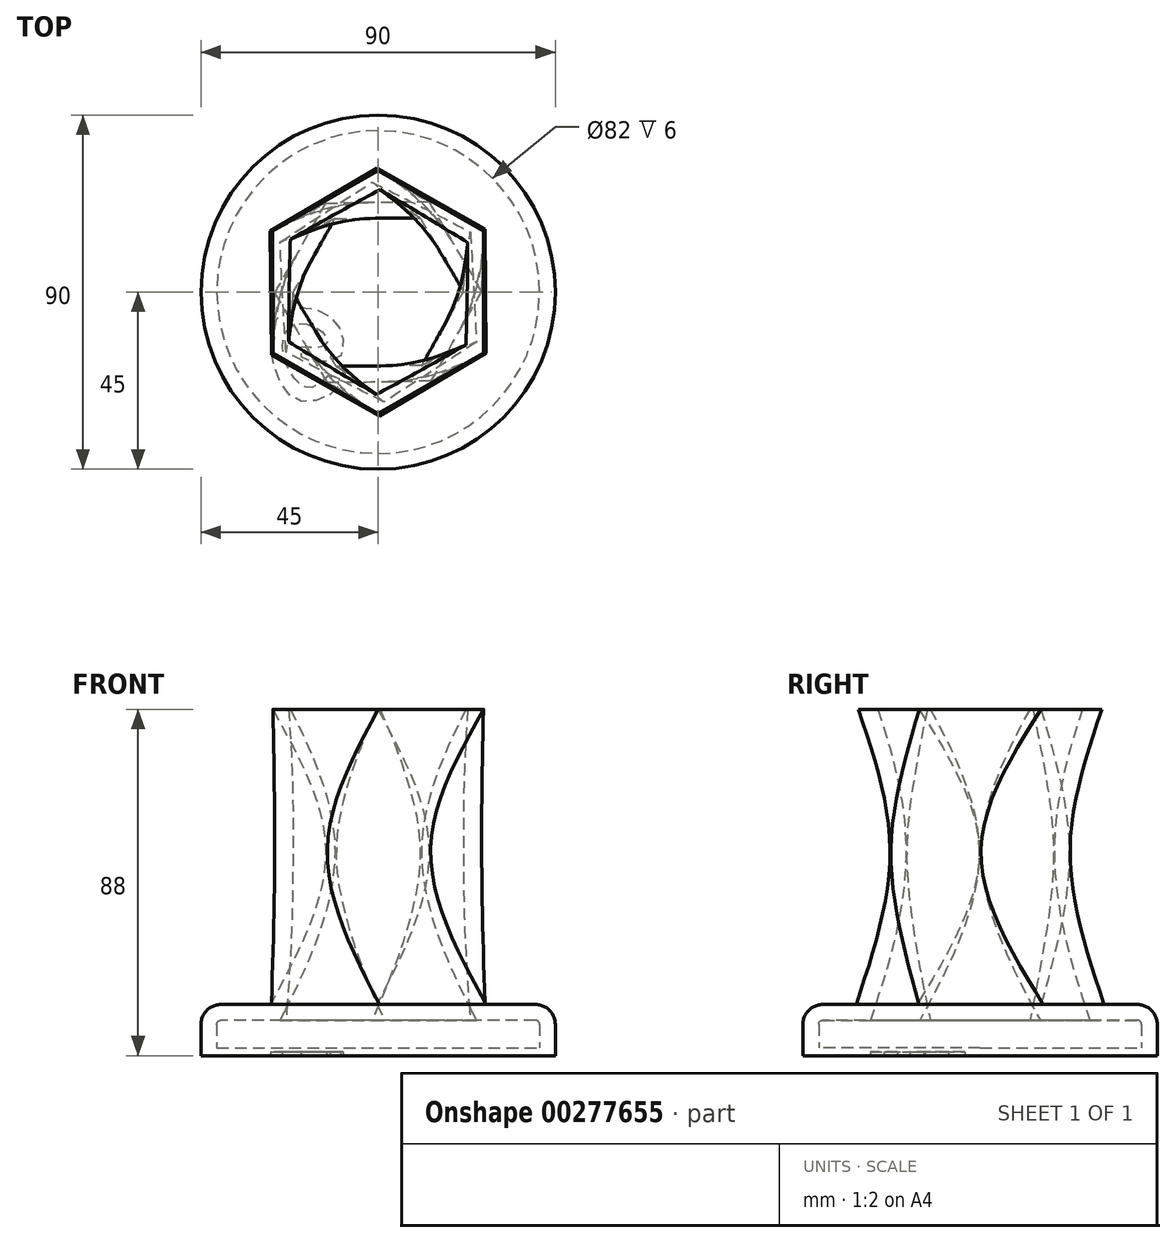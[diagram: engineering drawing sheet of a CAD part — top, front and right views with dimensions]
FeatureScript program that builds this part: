
annotation { "Feature Type Name" : "Feature", "Feature Type Description" : "" }
export const myFeature = defineFeature(function(context is Context, id is Id, definition is map)
    precondition{}
    {
        {
            var Q0;
            Q0=qCreatedBy(makeId("Top.planeOp"),FACE);
            var sketch = newSketch(context, id + "F0", { "sketchPlane" : qUnion([Q0])});
            skCircle(sketch, "E0", {"center": v(0, 0) * mm, "radius": 45 * mm});
            skSolve(sketch);
        }
        {
            var Q0;
            Q0 = qSketchRegion(id + "F0", true);
            extrude(context, id + "F1", {"entities" : qUnion([Q0]), "depth" : 15 * mm});
        }
        {
            var Q0;
            Q0=makeQuery(id+"F1.opExtrude","CAP_EDGE",EDGE,{"disambiguationData":[OSD([sQuery(id+"F0.wireOp",EDGE,"E0")])],"isStart":false});
            fillet(context, id + "F2", {"entities" : qUnion([Q0]), "radius" : 5 * mm, "tangentPropagation" : true, "allowEdgeOverflow" : false});
        }
        {
            var Q0;
            Q0=qCreatedBy(makeId("Top.planeOp"),FACE);
            cPlane(context, id + "F3", {"entities" : qUnion([Q0]), "cplaneType" : CPlaneType.OFFSET, "offset" : 15 * mm, "width" : 150 * mm, "height" : 150 * mm});
        }
        {
            var Q0;
            Q0=qCreatedBy(id+"F3.planeOp",FACE);
            var sketch = newSketch(context, id + "F4", { "sketchPlane" : qUnion([Q0])});
            skCircle(sketch, "E1.cCircle", {"center": v(0, 0) * mm, "radius": 27.26 * mm, "construction": true});
            skLineSegment(sketch, "E1.0", {"start": v(-0.3, 31.48) * mm, "end": v(27.1, 16) * mm});
            skLineSegment(sketch, "E1.1", {"start": v(27.1, 16) * mm, "end": v(27.4, -15.48) * mm});
            skLineSegment(sketch, "E1.2", {"start": v(27.4, -15.48) * mm, "end": v(0.3, -31.48) * mm});
            skLineSegment(sketch, "E1.3", {"start": v(0.3, -31.48) * mm, "end": v(-27.1, -16) * mm});
            skLineSegment(sketch, "E1.4", {"start": v(-27.1, -16) * mm, "end": v(-27.4, 15.48) * mm});
            skLineSegment(sketch, "E1.5", {"start": v(-27.4, 15.48) * mm, "end": v(-0.3, 31.48) * mm});
            skPoint(sketch, "E1.0.midPoint", {"position": v(13.4, 23.74) * mm});
            skSolve(sketch);
        }
        {
            var Q0;
            Q0=qCreatedBy(id+"F3.planeOp",FACE);
            cPlane(context, id + "F5", {"entities" : qUnion([Q0]), "cplaneType" : CPlaneType.OFFSET, "offset" : 40 * mm, "width" : 150 * mm, "height" : 150 * mm});
        }
        {
            var Q0;
            Q0=qCreatedBy(id+"F5.planeOp",FACE);
            var sketch = newSketch(context, id + "F6", { "sketchPlane" : qUnion([Q0])});
            skCircle(sketch, "E2.cCircle", {"center": v(0, 0) * mm, "radius": 22.76 * mm, "construction": true});
            skLineSegment(sketch, "E2.0", {"start": v(26.28, 0.28) * mm, "end": v(13.38, -22.62) * mm});
            skLineSegment(sketch, "E2.1", {"start": v(13.38, -22.62) * mm, "end": v(-12.9, -22.9) * mm});
            skLineSegment(sketch, "E2.2", {"start": v(-12.9, -22.9) * mm, "end": v(-26.28, -0.28) * mm});
            skLineSegment(sketch, "E2.3", {"start": v(-26.28, -0.28) * mm, "end": v(-13.38, 22.62) * mm});
            skLineSegment(sketch, "E2.4", {"start": v(-13.38, 22.62) * mm, "end": v(12.9, 22.9) * mm});
            skLineSegment(sketch, "E2.5", {"start": v(12.9, 22.9) * mm, "end": v(26.28, 0.28) * mm});
            skPoint(sketch, "E2.0.midPoint", {"position": v(19.83, -11.17) * mm});
            skSolve(sketch);
        }
        {
            var Q0;
            Q0=qCreatedBy(id+"F5.planeOp",FACE);
            cPlane(context, id + "F7", {"entities" : qUnion([Q0]), "cplaneType" : CPlaneType.OFFSET, "offset" : 35 * mm, "width" : 150 * mm, "height" : 150 * mm});
        }
        {
            var Q0;
            Q0=qCreatedBy(id+"F7.planeOp",FACE);
            var sketch = newSketch(context, id + "F8", { "sketchPlane" : qUnion([Q0])});
            skCircle(sketch, "E3.cCircle", {"center": v(0, 0) * mm, "radius": 26.78 * mm, "construction": true});
            skLineSegment(sketch, "E3.0", {"start": v(26.79, -15.44) * mm, "end": v(0.02, -30.92) * mm});
            skLineSegment(sketch, "E3.1", {"start": v(0.02, -30.92) * mm, "end": v(-26.76, -15.48) * mm});
            skLineSegment(sketch, "E3.2", {"start": v(-26.76, -15.48) * mm, "end": v(-26.79, 15.44) * mm});
            skLineSegment(sketch, "E3.3", {"start": v(-26.79, 15.44) * mm, "end": v(-0.02, 30.92) * mm});
            skLineSegment(sketch, "E3.4", {"start": v(-0.02, 30.92) * mm, "end": v(26.76, 15.48) * mm});
            skLineSegment(sketch, "E3.5", {"start": v(26.76, 15.48) * mm, "end": v(26.79, -15.44) * mm});
            skPoint(sketch, "E3.0.midPoint", {"position": v(13.4, -23.18) * mm});
            skSolve(sketch);
        }
        {
            var Q1;
            Q1=makeQuery(id+"F8.imprint","IMPRINT",FACE,{"disambiguationData":[TD([[makeQuery(id+"F8.imprint","IMPRINT",EDGE,{"derivedFrom":sQuery(id+"F8.wireOp",EDGE,"E3.0")}),-1.0]])]});
            var Q2;
            Q2=makeQuery(id+"F6.imprint","IMPRINT",FACE,{"disambiguationData":[TD([[makeQuery(id+"F6.imprint","IMPRINT",EDGE,{"derivedFrom":sQuery(id+"F6.wireOp",EDGE,"E2.0")}),-1.0]])]});
            var Q3;
            Q3=makeQuery(id+"F4.imprint","IMPRINT",FACE,{"disambiguationData":[TD([[makeQuery(id+"F4.imprint","IMPRINT",EDGE,{"derivedFrom":sQuery(id+"F4.wireOp",EDGE,"E1.0")}),-1.0]])]});
            loft(context, id + "F9", {"operationType" : NewBodyOperationType.ADD, "sheetProfilesArray" : [{ "sheetProfileEntities" : qUnion([Q1]) }, { "sheetProfileEntities" : qUnion([Q2]) }, { "sheetProfileEntities" : qUnion([Q3]) }]});
        }
        {
            var Q0;
            Q0=makeQuery(id+"F9.opLoft","CAP_FACE",FACE,{"disambiguationData":[OSD([makeQuery(id+"F8.imprint","IMPRINT",FACE,{"disambiguationData":[TD([[makeQuery(id+"F8.imprint","IMPRINT",EDGE,{"derivedFrom":sQuery(id+"F8.wireOp",EDGE,"E3.0")}),-1.0]])]})])],"isStart":true});
            shell(context, id + "F10", {"entities" : qUnion([Q0]), "thickness" : 4 * mm});
        }
        {
            var Q0;
            Q0=makeQuery(id+"F1.opExtrude","CAP_FACE",FACE,{"disambiguationData":[OSD([sQuery(id+"F0.wireOp",EDGE,"E0")])],"isStart":true});
            var sketch = newSketch(context, id + "F11", { "sketchPlane" : qUnion([Q0])});
            skFitSpline(sketch, "E4", {"points": [v(-19.62, 5.51) * mm, v(-3.35, 33.08) * mm, v(0, 13.82) * mm, v(15.25, 31.75) * mm, v(16.9, 0) * mm, v(17.57, 0) * mm], "startDerivative": vector(80.18, 181) * mm, "endDerivative": vector(19.84, 14.06) * mm});
            skFitSpline(sketch, "E5", {"points": [v(-19.62, 5.51) * mm, v(-13.86, 5.51) * mm, v(-9.38, 18.26) * mm, v(-4.37, 5.51) * mm, v(8.8, 13.78) * mm, v(11.18, -2.3) * mm, v(17.57, 0) * mm], "startDerivative": vector(53.31, -25.52) * mm, "endDerivative": vector(61.92, 48.85) * mm});
            skSolve(sketch);
        }
        {
            var Q0;
            Q0=makeQuery(id+"F11.imprint","IMPRINT",FACE,{"disambiguationData":[TD([[makeQuery(id+"F11.imprint","IMPRINT",EDGE,{"derivedFrom":sQuery(id+"F11.wireOp",EDGE,"E4")}),-1.0]])]});
            extrude(context, id + "F12", {"entities" : qUnion([Q0]), "operationType" : NewBodyOperationType.REMOVE, "oppositeDirection" : true, "depth" : 2 * mm});
        }
        {
            var Q0;
            Q0=makeQuery(id+"F1.opExtrude","CAP_FACE",FACE,{"disambiguationData":[OSD([sQuery(id+"F0.wireOp",EDGE,"E0")])],"isStart":true});
            extrude(context, id + "F13", {"entities" : qUnion([Q0]), "operationType" : NewBodyOperationType.REMOVE, "oppositeDirection" : true, "depth" : 2 * mm});
        }
        {
            var Q0;
            Q0=makeQuery(id+"F13.boolean.opBoolean","MERGE",FACE,{"derivedFrom":[makeQuery(id+"F12.boolean.opBoolean","COPY",FACE,{"derivedFrom":makeQuery(id+"F12.opExtrude","CAP_FACE",FACE,{"disambiguationData":[OSD([sQuery(id+"F11.wireOp",EDGE,"E4"),sQuery(id+"F11.wireOp",EDGE,"E5")])],"isStart":false})}),makeQuery(id+"F13.opExtrude","CAP_FACE",FACE,{"disambiguationData":[OSD([sQuery(id+"F0.wireOp",EDGE,"E0")])],"isStart":false})]});
            var sketch = newSketch(context, id + "F14", { "sketchPlane" : qUnion([Q0])});
            skFitSpline(sketch, "E6", {"points": [v(-12.29, 20.94) * mm, v(-17.31, 24.3) * mm, v(-21.78, 21.22) * mm, v(-24.3, 13.4) * mm, v(-20.94, 8.1) * mm, v(-13.68, 10.61) * mm, v(-13.4, 13.4) * mm, v(-19.55, 13.96) * mm], "startDerivative": vector(-34.9, 34.24) * mm, "endDerivative": vector(-53.39, -3.8) * mm});
            skFitSpline(sketch, "E7", {"points": [v(-12.29, 20.94) * mm, v(-9.63, 22.53) * mm, v(-12.29, 26.03) * mm, v(-20.24, 27.56) * mm, v(-25.68, 20.94) * mm, v(-27.22, 10.67) * mm, v(-24, 5.08) * mm, v(-14.24, 4.94) * mm, v(-9.07, 10.95) * mm, v(-9.07, 14.02) * mm, v(-9.9, 16.53) * mm, v(-18.7, 17.23) * mm, v(-19.55, 13.96) * mm], "startDerivative": vector(61.78, 20.43) * mm, "endDerivative": vector(7.27, -62.4) * mm});
            skSolve(sketch);
        }
        {
            var Q0;
            Q0=makeQuery(id+"F14.imprint","IMPRINT",FACE,{"disambiguationData":[TD([[makeQuery(id+"F14.imprint","IMPRINT",EDGE,{"derivedFrom":sQuery(id+"F14.wireOp",EDGE,"E6")}),-1.0]])]});
            extrude(context, id + "F15", {"entities" : qUnion([Q0]), "operationType" : NewBodyOperationType.REMOVE, "oppositeDirection" : true, "depth" : 1 * mm});
        }
    });
